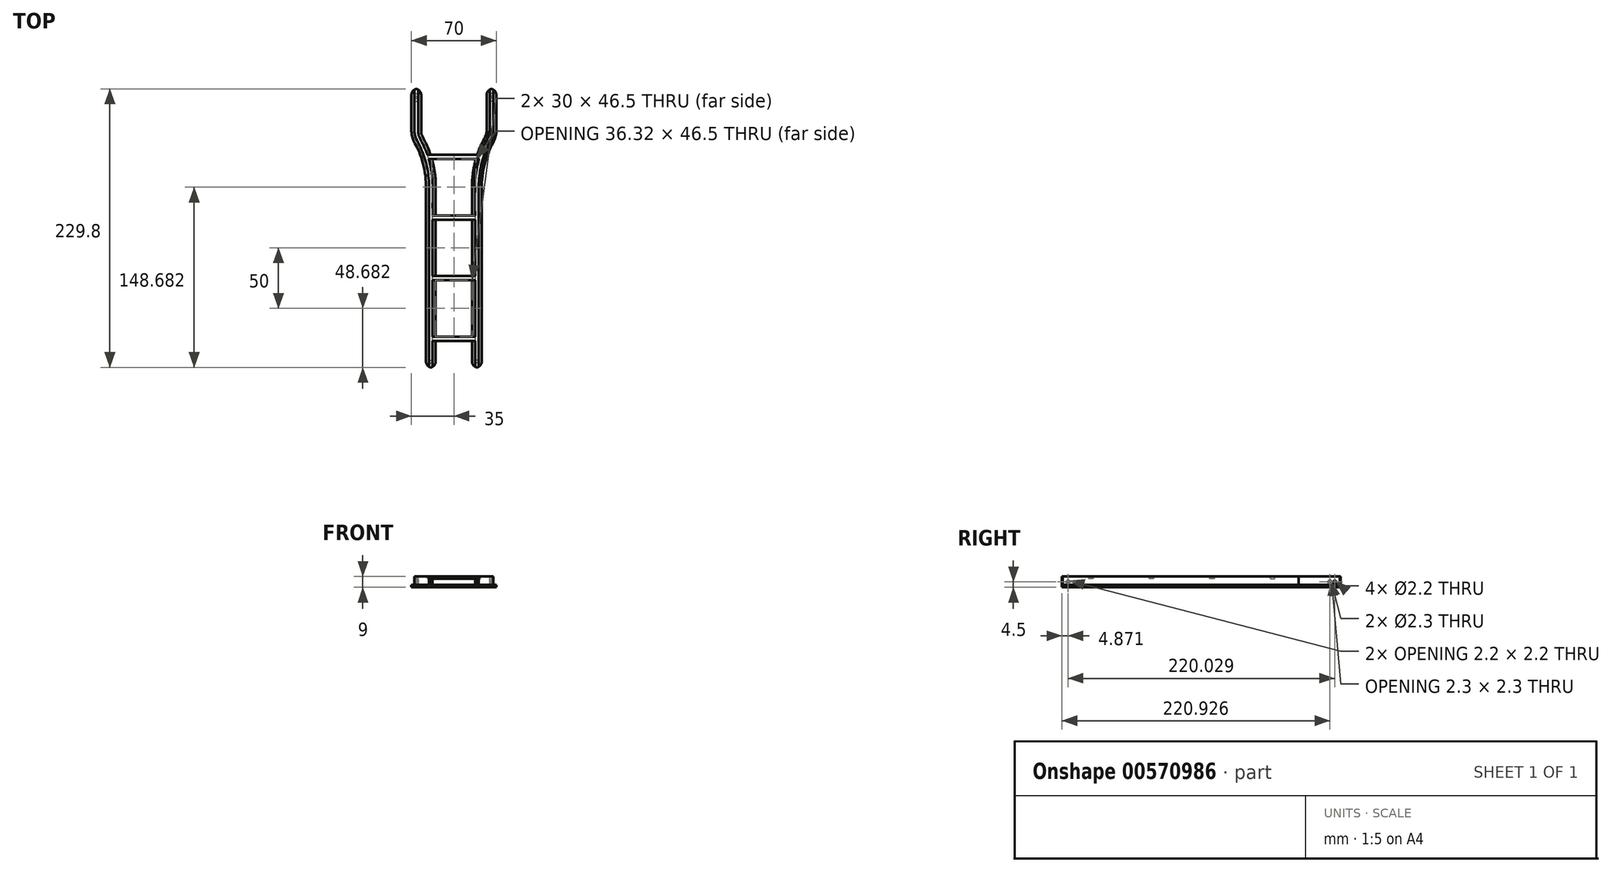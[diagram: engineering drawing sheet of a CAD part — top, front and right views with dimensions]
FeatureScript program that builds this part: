
annotation { "Feature Type Name" : "Feature", "Feature Type Description" : "" }
export const myFeature = defineFeature(function(context is Context, id is Id, definition is map)
    precondition{}
    {
        {
            var Q0;
            Q0=qCreatedBy(makeId("Front.planeOp"),FACE);
            var sketch = newSketch(context, id + "F0", { "sketchPlane" : qUnion([Q0])});
            skLineSegment(sketch, "E0.bottom", {"start": v(-15, 0) * mm, "end": v(-23, 0) * mm});
            skLineSegment(sketch, "E0.top", {"start": v(-15, 9) * mm, "end": v(-23, 9) * mm});
            skLineSegment(sketch, "E0.left", {"start": v(-15, 0) * mm, "end": v(-15, 2) * mm});
            skLineSegment(sketch, "E0.right", {"start": v(-23, 0) * mm, "end": v(-23, 2) * mm});
            skLineSegment(sketch, "E1.bottom", {"start": v(-23, 7) * mm, "end": v(-21, 7) * mm});
            skLineSegment(sketch, "E1.top", {"start": v(-23, 2) * mm, "end": v(-21, 2) * mm});
            skLineSegment(sketch, "E1.right", {"start": v(-20.5, 6.5) * mm, "end": v(-20.5, 2.5) * mm});
            skLineSegment(sketch, "E2.bottom", {"start": v(-17, 7) * mm, "end": v(-15, 7) * mm});
            skLineSegment(sketch, "E2.top", {"start": v(-17, 2) * mm, "end": v(-15, 2) * mm});
            skLineSegment(sketch, "E2.left", {"start": v(-17.5, 6.5) * mm, "end": v(-17.5, 2.5) * mm});
            skLineSegment(sketch, "E3", {"start": v(-19, 9) * mm, "end": v(-19, -4.59) * mm, "construction": true});
            skPoint(sketch, "E3.endSnap0", {"position": v(-19, 0) * mm});
            skLineSegment(sketch, "E4.trimOffspring", {"start": v(-15, 7) * mm, "end": v(-15, 9) * mm});
            skLineSegment(sketch, "E5.trimOffspring", {"start": v(-23, 7) * mm, "end": v(-23, 9) * mm});
            skPoint(sketch, "E6.visualSharp", {"position": v(-20.5, 7) * mm});
            skArc(sketch, "E6.filletArc", {"start": v(-20.5, 6.5) * mm, "mid": v(-20.65, 6.85) * mm, "end": v(-21, 7) * mm});
            skPoint(sketch, "E7.visualSharp", {"position": v(-17.5, 7) * mm});
            skArc(sketch, "E7.filletArc", {"start": v(-17, 7) * mm, "mid": v(-17.35, 6.85) * mm, "end": v(-17.5, 6.5) * mm});
            skPoint(sketch, "E8.visualSharp", {"position": v(-17.5, 2) * mm});
            skArc(sketch, "E8.filletArc", {"start": v(-17.5, 2.5) * mm, "mid": v(-17.35, 2.15) * mm, "end": v(-17, 2) * mm});
            skPoint(sketch, "E9.visualSharp", {"position": v(-20.5, 2) * mm});
            skArc(sketch, "E9.filletArc", {"start": v(-21, 2) * mm, "mid": v(-20.65, 2.15) * mm, "end": v(-20.5, 2.5) * mm});
            skSolve(sketch);
        }
        {
            var Q0;
            Q0=qCreatedBy(makeId("Top.planeOp"),FACE);
            var sketch = newSketch(context, id + "F1", { "sketchPlane" : qUnion([Q0])});
            skLineSegment(sketch, "E10", {"start": v(-35.26, 0) * mm, "end": v(-35.26, 150) * mm});
            skLineSegment(sketch, "E11", {"start": v(-47.26, 230) * mm, "end": v(-47.26, 195) * mm});
            skFitSpline(sketch, "E12", {"points": [v(-35.26, 150) * mm, v(-40.7, 174.86) * mm, v(-47.26, 195) * mm], "startDerivative": vector(-0.38, 53.31) * mm, "endDerivative": vector(-0.87, 58.08) * mm});
            skSolve(sketch);
        }
        {
            var Q0;
            Q0=qSketchRegion(id+"F0",true);
            var Q1;
            Q1=qConstructionFilter(qBodyType(qCreatedBy(id+"F1",EDGE),BodyType.WIRE),ConstructionObject.NO);
            sweep(context, id + "F2", {"profiles" : qUnion([Q0]), "path" : qUnion([Q1])});
        }
        {
            var Q0;
            Q0=qCreatedBy(makeId("Front.planeOp"),FACE);
            var sketch = newSketch(context, id + "F3", { "sketchPlane" : qUnion([Q0])});
            skLineSegment(sketch, "E13.bottom", {"start": v(-17.5, 6.31) * mm, "end": v(-14.7, 6.31) * mm});
            skLineSegment(sketch, "E13.top", {"start": v(-17.5, 10.3) * mm, "end": v(-14.7, 10.3) * mm});
            skLineSegment(sketch, "E13.left", {"start": v(-17.5, 6.31) * mm, "end": v(-17.5, 10.3) * mm});
            skLineSegment(sketch, "E13.right", {"start": v(-14.7, 6.31) * mm, "end": v(-14.7, 10.3) * mm});
            skLineSegment(sketch, "E14.bottom", {"start": v(-20.5, 6.31) * mm, "end": v(-23, 6.31) * mm});
            skLineSegment(sketch, "E14.top", {"start": v(-20.5, 10.3) * mm, "end": v(-23, 10.3) * mm});
            skLineSegment(sketch, "E14.left", {"start": v(-20.5, 6.31) * mm, "end": v(-20.5, 10.3) * mm});
            skLineSegment(sketch, "E14.right", {"start": v(-23, 6.31) * mm, "end": v(-23, 10.3) * mm});
            skSolve(sketch);
        }
        {
            var Q0;
            Q0=makeQuery(id+"F2.opSweep","SWEPT_FACE",FACE,{"disambiguationData":[OSD([sQuery(id+"F0.wireOp",EDGE,"E4.trimOffspring"),sQuery(id+"F1.wireOp",EDGE,"E10")])]});
            var sketch = newSketch(context, id + "F4", { "sketchPlane" : qUnion([Q0])});
            skLineSegment(sketch, "E15.bottom", {"start": v(22.03, 9) * mm, "end": v(25.53, 9) * mm});
            skLineSegment(sketch, "E15.top", {"start": v(22.03, 7) * mm, "end": v(25.53, 7) * mm});
            skLineSegment(sketch, "E15.left", {"start": v(22.03, 9) * mm, "end": v(22.03, 7) * mm});
            skLineSegment(sketch, "E15.right", {"start": v(25.53, 9) * mm, "end": v(25.53, 7) * mm});
            skLineSegment(sketch, "E16.0.1.0", {"start": v(22.03, 2) * mm, "end": v(22.03, 0) * mm});
            skLineSegment(sketch, "E16.0.1.1", {"start": v(22.03, 0) * mm, "end": v(25.53, 0) * mm});
            skLineSegment(sketch, "E16.0.1.2", {"start": v(22.03, 2) * mm, "end": v(25.53, 2) * mm});
            skLineSegment(sketch, "E16.0.1.3", {"start": v(25.53, 2) * mm, "end": v(25.53, 0) * mm});
            skLineSegment(sketch, "E16.1.0.0", {"start": v(72.03, 9) * mm, "end": v(72.03, 7) * mm});
            skLineSegment(sketch, "E16.1.0.1", {"start": v(72.03, 7) * mm, "end": v(75.53, 7) * mm});
            skLineSegment(sketch, "E16.1.0.2", {"start": v(72.03, 9) * mm, "end": v(75.53, 9) * mm});
            skLineSegment(sketch, "E16.1.0.3", {"start": v(75.53, 9) * mm, "end": v(75.53, 7) * mm});
            skLineSegment(sketch, "E16.1.1.0", {"start": v(72.03, 2) * mm, "end": v(72.03, 0) * mm});
            skLineSegment(sketch, "E16.1.1.1", {"start": v(72.03, 0) * mm, "end": v(75.53, 0) * mm});
            skLineSegment(sketch, "E16.1.1.2", {"start": v(72.03, 2) * mm, "end": v(75.53, 2) * mm});
            skLineSegment(sketch, "E16.1.1.3", {"start": v(75.53, 2) * mm, "end": v(75.53, 0) * mm});
            skLineSegment(sketch, "E16.2.0.0", {"start": v(122.03, 9) * mm, "end": v(122.03, 7) * mm});
            skLineSegment(sketch, "E16.2.0.1", {"start": v(122.03, 7) * mm, "end": v(125.53, 7) * mm});
            skLineSegment(sketch, "E16.2.0.2", {"start": v(122.03, 9) * mm, "end": v(125.53, 9) * mm});
            skLineSegment(sketch, "E16.2.0.3", {"start": v(125.53, 9) * mm, "end": v(125.53, 7) * mm});
            skLineSegment(sketch, "E16.2.1.0", {"start": v(122.03, 2) * mm, "end": v(122.03, 0) * mm});
            skLineSegment(sketch, "E16.2.1.1", {"start": v(122.03, 0) * mm, "end": v(125.53, 0) * mm});
            skLineSegment(sketch, "E16.2.1.2", {"start": v(122.03, 2) * mm, "end": v(125.53, 2) * mm});
            skLineSegment(sketch, "E16.2.1.3", {"start": v(125.53, 2) * mm, "end": v(125.53, 0) * mm});
            skLineSegment(sketch, "E16.3.0.0", {"start": v(172.03, 9) * mm, "end": v(172.03, 7) * mm});
            skLineSegment(sketch, "E16.3.0.1", {"start": v(172.03, 7) * mm, "end": v(175.53, 7) * mm});
            skLineSegment(sketch, "E16.3.0.2", {"start": v(172.03, 9) * mm, "end": v(175.53, 9) * mm});
            skLineSegment(sketch, "E16.3.0.3", {"start": v(175.53, 9) * mm, "end": v(175.53, 7) * mm});
            skLineSegment(sketch, "E16.3.1.0", {"start": v(172.03, 2) * mm, "end": v(172.03, 0) * mm});
            skLineSegment(sketch, "E16.3.1.1", {"start": v(172.03, 0) * mm, "end": v(175.53, 0) * mm});
            skLineSegment(sketch, "E16.3.1.2", {"start": v(172.03, 2) * mm, "end": v(175.53, 2) * mm});
            skLineSegment(sketch, "E16.3.1.3", {"start": v(175.53, 2) * mm, "end": v(175.53, 0) * mm});
            skLineSegment(sketch, "E16.direction1", {"start": v(22.03, 7) * mm, "end": v(72.03, 7) * mm, "construction": true});
            skLineSegment(sketch, "E16.direction2", {"start": v(22.03, 7) * mm, "end": v(22.03, 0) * mm, "construction": true});
            skSolve(sketch);
        }
        {
            var Q0;
            Q0=qSketchRegion(id+"F4",true);
            extrude(context, id + "F5", {"entities" : qUnion([Q0]), "operationType" : NewBodyOperationType.ADD, "depth" : 15 * mm});
        }
        {
            var Q0;
            Q0=makeQuery(id+"F5.opExtrude","CAP_FACE",FACE,{"disambiguationData":[OSD([sQuery(id+"F4.wireOp",EDGE,"E16.3.0.0"),sQuery(id+"F4.wireOp",EDGE,"E16.3.0.1"),sQuery(id+"F4.wireOp",EDGE,"E16.3.0.2"),sQuery(id+"F4.wireOp",EDGE,"E16.3.0.3")])],"isStart":true});
            var sketch = newSketch(context, id + "F6", { "sketchPlane" : qUnion([Q0])});
            skLineSegment(sketch, "E17.0", {"start": v(-172.03, 7) * mm, "end": v(-175.53, 7) * mm});
            skLineSegment(sketch, "E18.0.0", {"start": v(-175.53, 9) * mm, "end": v(-175.53, 7) * mm});
            skLineSegment(sketch, "E18.0.1", {"start": v(-175.53, 7) * mm, "end": v(-172.03, 7) * mm});
            skLineSegment(sketch, "E18.0.2", {"start": v(-172.03, 7) * mm, "end": v(-172.03, 9) * mm});
            skLineSegment(sketch, "E18.0.3", {"start": v(-172.03, 9) * mm, "end": v(-175.53, 9) * mm});
            skLineSegment(sketch, "E19.0.0", {"start": v(-175.53, 2) * mm, "end": v(-175.53, 0) * mm});
            skLineSegment(sketch, "E19.0.1", {"start": v(-175.53, 0) * mm, "end": v(-172.03, 0) * mm});
            skLineSegment(sketch, "E19.0.2", {"start": v(-172.03, 0) * mm, "end": v(-172.03, 2) * mm});
            skLineSegment(sketch, "E19.0.3", {"start": v(-172.03, 2) * mm, "end": v(-175.53, 2) * mm});
            skSolve(sketch);
        }
        {
            var Q0;
            Q0=qSketchRegion(id+"F6",true);
            extrude(context, id + "F7", {"entities" : qUnion([Q0]), "operationType" : NewBodyOperationType.ADD, "endBound" : BoundingType.UP_TO_NEXT, "depth" : 25 * mm});
        }
        {
            var Q0;
            Q0=qSketchRegion(id+"F3",true);
            var Q1;
            Q1=qConstructionFilter(qBodyType(qCreatedBy(id+"F1",EDGE),BodyType.WIRE),ConstructionObject.NO);
            sweep(context, id + "F8", {"operationType" : NewBodyOperationType.REMOVE, "profiles" : qUnion([Q0]), "path" : qUnion([Q1])});
        }
        {
            var Q0;
            Q0=qCreatedBy(makeId("Right.planeOp"),FACE);
            var sketch = newSketch(context, id + "F9", { "sketchPlane" : qUnion([Q0])});
            skLineSegment(sketch, "E20.0.0", {"start": v(25.53, 7) * mm, "end": v(25.53, 9) * mm});
            skLineSegment(sketch, "E20.0.1", {"start": v(25.53, 9) * mm, "end": v(22.03, 9) * mm});
            skLineSegment(sketch, "E20.0.2", {"start": v(22.03, 9) * mm, "end": v(22.03, 7) * mm});
            skLineSegment(sketch, "E20.0.3", {"start": v(22.03, 7) * mm, "end": v(25.53, 7) * mm});
            skLineSegment(sketch, "E21.0.0", {"start": v(75.53, 7) * mm, "end": v(75.53, 9) * mm});
            skLineSegment(sketch, "E21.0.1", {"start": v(75.53, 9) * mm, "end": v(72.03, 9) * mm});
            skLineSegment(sketch, "E21.0.2", {"start": v(72.03, 9) * mm, "end": v(72.03, 7) * mm});
            skLineSegment(sketch, "E21.0.3", {"start": v(72.03, 7) * mm, "end": v(75.53, 7) * mm});
            skLineSegment(sketch, "E22.0.0", {"start": v(175.53, 7) * mm, "end": v(175.53, 9) * mm});
            skLineSegment(sketch, "E22.0.1", {"start": v(175.53, 9) * mm, "end": v(172.03, 9) * mm});
            skLineSegment(sketch, "E22.0.2", {"start": v(172.03, 9) * mm, "end": v(172.03, 7) * mm});
            skLineSegment(sketch, "E22.0.3", {"start": v(172.03, 7) * mm, "end": v(175.53, 7) * mm});
            skLineSegment(sketch, "E23.0.0", {"start": v(125.53, 7) * mm, "end": v(125.53, 9) * mm});
            skLineSegment(sketch, "E23.0.1", {"start": v(125.53, 9) * mm, "end": v(122.03, 9) * mm});
            skLineSegment(sketch, "E23.0.2", {"start": v(122.03, 9) * mm, "end": v(122.03, 7) * mm});
            skLineSegment(sketch, "E23.0.3", {"start": v(122.03, 7) * mm, "end": v(125.53, 7) * mm});
            skSolve(sketch);
        }
        {
            var Q0;
            Q0=qSketchRegion(id+"F9",true);
            var Q1;
            Q1=makeQuery(id+"F8.boolean.opBoolean","SPLIT",BODY,{"disambiguationData":[OD(0.0)],"derivedFrom":makeQuery(id+"F2.opSweep","SWEPT_BODY",BODY,{"disambiguationData":[OSD([sQuery(id+"F0.wireOp",EDGE,"E0.bottom"),sQuery(id+"F0.wireOp",EDGE,"E0.top"),sQuery(id+"F0.wireOp",EDGE,"E0.left"),sQuery(id+"F0.wireOp",EDGE,"E0.right"),sQuery(id+"F0.wireOp",EDGE,"E1.bottom"),sQuery(id+"F0.wireOp",EDGE,"E1.top"),sQuery(id+"F0.wireOp",EDGE,"E1.right"),sQuery(id+"F0.wireOp",EDGE,"E2.bottom"),sQuery(id+"F0.wireOp",EDGE,"E2.top"),sQuery(id+"F0.wireOp",EDGE,"E2.left"),sQuery(id+"F0.wireOp",EDGE,"E4.trimOffspring"),sQuery(id+"F0.wireOp",EDGE,"E5.trimOffspring"),sQuery(id+"F0.wireOp",EDGE,"E6.filletArc"),sQuery(id+"F0.wireOp",EDGE,"E7.filletArc"),sQuery(id+"F0.wireOp",EDGE,"E8.filletArc"),sQuery(id+"F0.wireOp",EDGE,"E9.filletArc"),sQuery(id+"F1.wireOp",EDGE,"E11")])]})});
            extrude(context, id + "F10", {"entities" : qUnion([Q0]), "operationType" : NewBodyOperationType.ADD, "endBound" : BoundingType.UP_TO_BODY, "oppositeDirection" : true, "depth" : 25 * mm, "endBoundEntityBody" : qUnion([Q1]), "offsetDistance" : 25 * mm});
        }
        {
            var Q0;
            {var subQ0=sQuery(id+"F1.wireOp",EDGE,"E10");Q0=makeQuery(id+"F8.boolean.opBoolean","MERGE",FACE,{"derivedFrom":[makeQuery(id+"F2.opSweep","SWEPT_FACE",FACE,{"disambiguationData":[OSD([sQuery(id+"F0.wireOp",EDGE,"E2.left"),subQ0])]}),makeQuery(id+"F8.opSweep","SWEPT_FACE",FACE,{"disambiguationData":[OSD([subQ0,sQuery(id+"F3.wireOp",EDGE,"E13.left")])]})]});}
            var sketch = newSketch(context, id + "F11", { "sketchPlane" : qUnion([Q0])});
            skCircle(sketch, "E24", {"center": v(4.97, 4.5) * mm, "radius": 1.1 * mm});
            skCircle(sketch, "E25", {"center": v(225, 4.5) * mm, "radius": 1.1 * mm});
            skCircle(sketch, "E26", {"center": v(221.03, 4.5) * mm, "radius": 1.15 * mm});
            skSolve(sketch);
        }
        {
            var Q0;
            Q0=qSketchRegion(id+"F11",true);
            extrude(context, id + "F12", {"entities" : qUnion([Q0]), "operationType" : NewBodyOperationType.REMOVE, "endBound" : BoundingType.THROUGH_ALL, "oppositeDirection" : true, "depth" : 25 * mm, "offsetDistance" : 25 * mm});
        }
        {
            var Q0;
            Q0=makeQuery(id+"F2.opSweep","CAP_EDGE",EDGE,{"disambiguationData":[OSD([sQuery(id+"F0.wireOp",EDGE,"E0.left"),sQuery(id+"F1.wireOp",VERTEX,"E10.start")])],"isStart":true});
            var Q1;
            Q1=makeQuery(id+"F2.opSweep","CAP_EDGE",EDGE,{"disambiguationData":[OSD([sQuery(id+"F0.wireOp",EDGE,"E0.right"),sQuery(id+"F1.wireOp",VERTEX,"E10.start")])],"isStart":true});
            var Q2;
            Q2=makeQuery(id+"F2.opSweep","CAP_EDGE",EDGE,{"disambiguationData":[OSD([sQuery(id+"F0.wireOp",EDGE,"E0.right"),sQuery(id+"F1.wireOp",VERTEX,"E11.start")])],"isStart":false});
            var Q3;
            Q3=makeQuery(id+"F2.opSweep","CAP_EDGE",EDGE,{"disambiguationData":[OSD([sQuery(id+"F0.wireOp",EDGE,"E0.left"),sQuery(id+"F1.wireOp",VERTEX,"E11.start")])],"isStart":false});
            fillet(context, id + "F13", {"entities" : qUnion([Q0, Q1, Q2, Q3]), "radius" : 5 * mm, "tangentPropagation" : true, "allowEdgeOverflow" : false});
        }
        {
            var Q0;
            Q0=makeQuery(id+"F8.boolean.opBoolean","SPLIT",BODY,{"disambiguationData":[OD(0.0)],"derivedFrom":makeQuery(id+"F2.opSweep","SWEPT_BODY",BODY,{"disambiguationData":[OSD([sQuery(id+"F0.wireOp",EDGE,"E0.bottom"),sQuery(id+"F0.wireOp",EDGE,"E0.top"),sQuery(id+"F0.wireOp",EDGE,"E0.left"),sQuery(id+"F0.wireOp",EDGE,"E0.right"),sQuery(id+"F0.wireOp",EDGE,"E1.bottom"),sQuery(id+"F0.wireOp",EDGE,"E1.top"),sQuery(id+"F0.wireOp",EDGE,"E1.right"),sQuery(id+"F0.wireOp",EDGE,"E2.bottom"),sQuery(id+"F0.wireOp",EDGE,"E2.top"),sQuery(id+"F0.wireOp",EDGE,"E2.left"),sQuery(id+"F0.wireOp",EDGE,"E4.trimOffspring"),sQuery(id+"F0.wireOp",EDGE,"E5.trimOffspring"),sQuery(id+"F0.wireOp",EDGE,"E6.filletArc"),sQuery(id+"F0.wireOp",EDGE,"E7.filletArc"),sQuery(id+"F0.wireOp",EDGE,"E8.filletArc"),sQuery(id+"F0.wireOp",EDGE,"E9.filletArc"),sQuery(id+"F1.wireOp",EDGE,"E11")])]})});
            var Q1;
            Q1=makeQuery(id+"F5.opExtrude","CAP_FACE",FACE,{"disambiguationData":[OSD([sQuery(id+"F4.wireOp",EDGE,"E15.bottom"),sQuery(id+"F4.wireOp",EDGE,"E15.top"),sQuery(id+"F4.wireOp",EDGE,"E15.left"),sQuery(id+"F4.wireOp",EDGE,"E15.right")])],"isStart":false});
            mirror(context, id + "F14", {"operationType" : NewBodyOperationType.ADD, "entities" : qUnion([Q0]), "mirrorPlane" : qUnion([Q1])});
        }
    });
